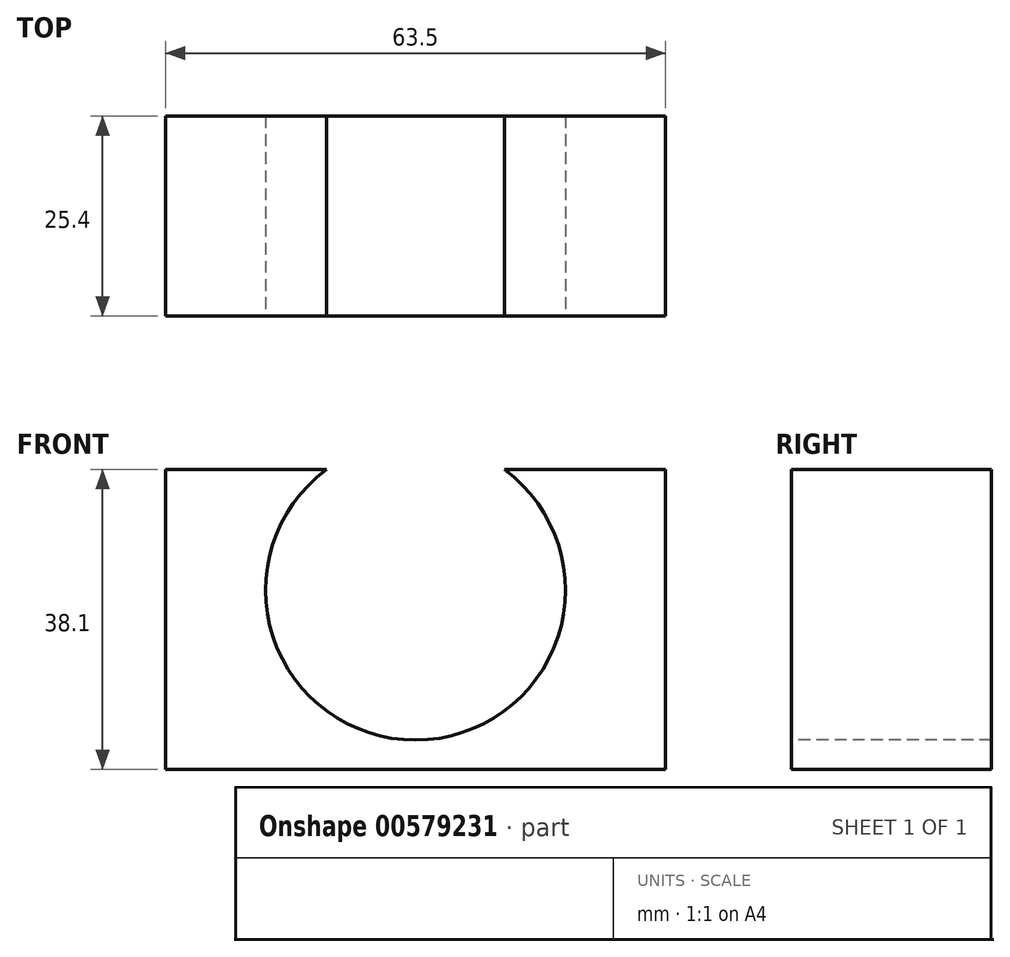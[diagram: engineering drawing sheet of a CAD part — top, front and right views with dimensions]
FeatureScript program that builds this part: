
annotation { "Feature Type Name" : "Feature", "Feature Type Description" : "" }
export const myFeature = defineFeature(function(context is Context, id is Id, definition is map)
    precondition{}
    {
        {
            var Q0;
            Q0=qCreatedBy(makeId("Front.planeOp"),FACE);
            var sketch = newSketch(context, id + "F0", { "sketchPlane" : qUnion([Q0])});
            skLineSegment(sketch, "E0", {"start": v(-39.71, 33.43) * mm, "end": v(23.79, 33.43) * mm});
            skLineSegment(sketch, "E1", {"start": v(23.79, 33.43) * mm, "end": v(23.79, -4.67) * mm});
            skLineSegment(sketch, "E2", {"start": v(-39.71, 33.43) * mm, "end": v(-39.71, -4.67) * mm});
            skLineSegment(sketch, "E3", {"start": v(-39.71, -4.67) * mm, "end": v(23.79, -4.67) * mm});
            skSolve(sketch);
        }
        {
            var Q0;
            Q0=makeQuery(id+"F0.imprint","IMPRINT",FACE,{"disambiguationData":[TD([[makeQuery(id+"F0.imprint","IMPRINT",EDGE,{"derivedFrom":sQuery(id+"F0.wireOp",EDGE,"E0")}),-1.0]])]});
            extrude(context, id + "F1", {"entities" : qUnion([Q0]), "oppositeDirection" : true, "depth" : 25.4 * mm, "offsetDistance" : 25.4 * mm});
        }
        {
            var Q0;
            Q0=makeQuery(id+"F1.opExtrude","CAP_FACE",FACE,{"disambiguationData":[OSD([sQuery(id+"F0.wireOp",EDGE,"E0"),sQuery(id+"F0.wireOp",EDGE,"E1"),sQuery(id+"F0.wireOp",EDGE,"E2"),sQuery(id+"F0.wireOp",EDGE,"E3")])],"isStart":true});
            var sketch = newSketch(context, id + "F2", { "sketchPlane" : qUnion([Q0])});
            skCircle(sketch, "E4", {"center": v(-7.96, 18.1) * mm, "radius": 19.05 * mm});
            skPoint(sketch, "E4.centerSnap0", {"position": v(-7.96, 33.43) * mm});
            skSolve(sketch);
        }
        {
            var Q0;
            {var subQ0=sQuery(id+"F2.wireOp",EDGE,"E4");var subQ1=makeQuery(id+"F1.opExtrude","CAP_EDGE",EDGE,{"disambiguationData":[OSD([sQuery(id+"F0.wireOp",EDGE,"E0")])],"isStart":true});var subQ2=makeQuery(id+"F2.imprint","INTERSECT",VERTEX,{"disambiguationData":[OD(0.0)],"derivedFrom":[subQ1,subQ0]});Q0=makeQuery(id+"F2.imprint","IMPRINT",FACE,{"disambiguationData":[TD([[makeQuery(id+"F2.imprint","IMPRINT",EDGE,{"disambiguationData":[TD([[subQ2,-1.0]])],"derivedFrom":subQ0}),1.0]])]});}
            extrude(context, id + "F3", {"entities" : qUnion([Q0]), "operationType" : NewBodyOperationType.REMOVE, "oppositeDirection" : true, "depth" : 25.4 * mm, "offsetDistance" : 25.4 * mm});
        }
    });
